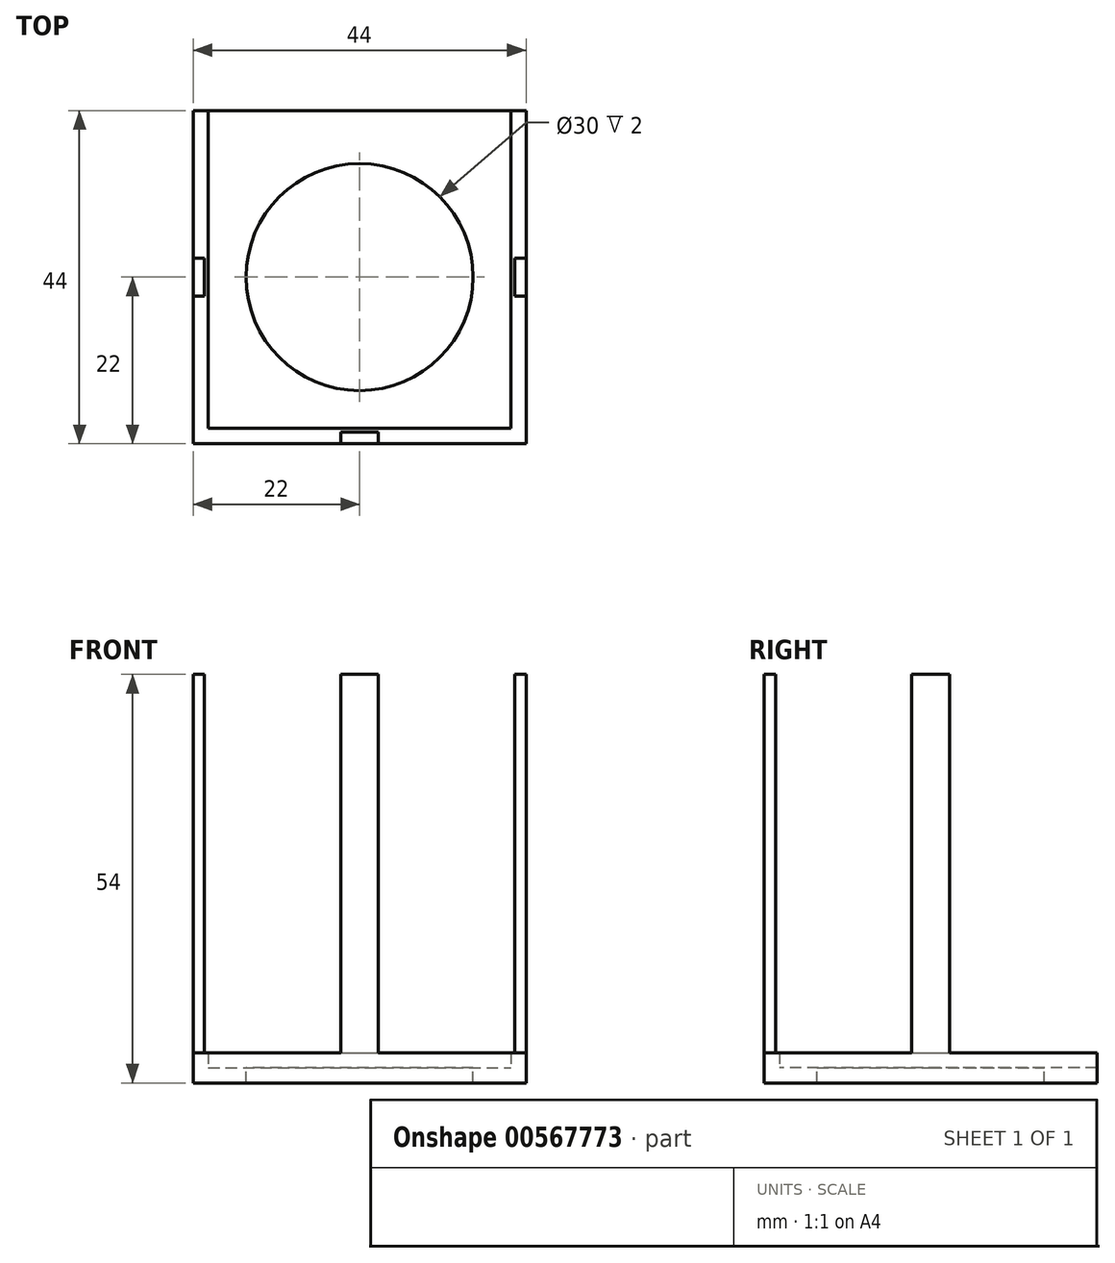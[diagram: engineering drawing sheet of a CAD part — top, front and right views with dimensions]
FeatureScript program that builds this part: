
annotation { "Feature Type Name" : "Feature", "Feature Type Description" : "" }
export const myFeature = defineFeature(function(context is Context, id is Id, definition is map)
    precondition{}
    {
        {
            var Q0;
            Q0=qCreatedBy(makeId("Top.planeOp"),FACE);
            var sketch = newSketch(context, id + "F0", { "sketchPlane" : qUnion([Q0])});
            skLineSegment(sketch, "E0.bottom", {"start": v(-22, 22) * mm, "end": v(22, 22) * mm});
            skLineSegment(sketch, "E0.top", {"start": v(-22, -22) * mm, "end": v(22, -22) * mm});
            skLineSegment(sketch, "E0.left", {"start": v(-22, 22) * mm, "end": v(-22, -22) * mm});
            skLineSegment(sketch, "E0.right", {"start": v(22, 22) * mm, "end": v(22, -22) * mm});
            skPoint(sketch, "E0.middle", {"position": v(0, 0) * mm});
            skCircle(sketch, "E1", {"center": v(0, 0) * mm, "radius": 15 * mm});
            skLineSegment(sketch, "E2", {"start": v(-20, 22) * mm, "end": v(-20, -20) * mm});
            skLineSegment(sketch, "E3", {"start": v(-20, -20) * mm, "end": v(20, -20) * mm});
            skLineSegment(sketch, "E4", {"start": v(20, -20) * mm, "end": v(20, 22) * mm});
            skSolve(sketch);
        }
        {
            var Q0;
            Q0=makeQuery(id+"F0.imprint","IMPRINT",FACE,{"disambiguationData":[TD([[makeQuery(id+"F0.imprint","IMPRINT",EDGE,{"derivedFrom":sQuery(id+"F0.wireOp",EDGE,"E1")}),-1.0]])]});
            var Q1;
            Q1=makeQuery(id+"F0.imprint","IMPRINT",FACE,{"disambiguationData":[TD([[makeQuery(id+"F0.imprint","IMPRINT",EDGE,{"derivedFrom":sQuery(id+"F0.wireOp",EDGE,"E0.bottom")}),-1.0]])]});
            extrude(context, id + "F1", {"entities" : qUnion([Q0, Q1]), "oppositeDirection" : true, "depth" : 2 * mm, "offsetDistance" : 25 * mm});
        }
        {
            var Q0;
            Q0=makeQuery(id+"F0.imprint","IMPRINT",FACE,{"disambiguationData":[TD([[makeQuery(id+"F0.imprint","IMPRINT",EDGE,{"derivedFrom":sQuery(id+"F0.wireOp",EDGE,"E0.top")}),1.0]])]});
            extrude(context, id + "F2", {"entities" : qUnion([Q0]), "operationType" : NewBodyOperationType.ADD, "depth" : 2 * mm, "offsetDistance" : 25 * mm});
        }
        {
            var Q0;
            Q0=makeQuery(id+"F2.opExtrude","CAP_FACE",FACE,{"disambiguationData":[OSD([sQuery(id+"F0.wireOp",EDGE,"E0.bottom"),sQuery(id+"F0.wireOp",EDGE,"E0.top"),sQuery(id+"F0.wireOp",EDGE,"E0.left"),sQuery(id+"F0.wireOp",EDGE,"E0.right"),sQuery(id+"F0.wireOp",EDGE,"E2"),sQuery(id+"F0.wireOp",EDGE,"E3"),sQuery(id+"F0.wireOp",EDGE,"E4")])],"isStart":false});
            var sketch = newSketch(context, id + "F3", { "sketchPlane" : qUnion([Q0])});
            skLineSegment(sketch, "E5.bottom", {"start": v(-22, 2.5) * mm, "end": v(-20.5, 2.5) * mm});
            skLineSegment(sketch, "E5.top", {"start": v(-22, -2.5) * mm, "end": v(-20.5, -2.5) * mm});
            skLineSegment(sketch, "E5.left", {"start": v(-22, 2.5) * mm, "end": v(-22, -2.5) * mm});
            skLineSegment(sketch, "E5.right", {"start": v(-20.5, 2.5) * mm, "end": v(-20.5, -2.5) * mm});
            skPoint(sketch, "E5.middle", {"position": v(-21.25, 0) * mm});
            skLineSegment(sketch, "E6.1.0", {"start": v(-2.5, -20.5) * mm, "end": v(2.5, -20.5) * mm});
            skPoint(sketch, "E6.1.1", {"position": v(0, -21.25) * mm});
            skLineSegment(sketch, "E6.1.2", {"start": v(-2.5, -22) * mm, "end": v(2.5, -22) * mm});
            skLineSegment(sketch, "E6.1.3", {"start": v(2.5, -22) * mm, "end": v(2.5, -20.5) * mm});
            skLineSegment(sketch, "E6.1.4", {"start": v(-2.5, -22) * mm, "end": v(-2.5, -20.5) * mm});
            skLineSegment(sketch, "E6.2.0", {"start": v(20.5, -2.5) * mm, "end": v(20.5, 2.5) * mm});
            skPoint(sketch, "E6.2.1", {"position": v(21.25, 0) * mm});
            skLineSegment(sketch, "E6.2.2", {"start": v(22, -2.5) * mm, "end": v(22, 2.5) * mm});
            skLineSegment(sketch, "E6.2.3", {"start": v(22, 2.5) * mm, "end": v(20.5, 2.5) * mm});
            skLineSegment(sketch, "E6.2.4", {"start": v(22, -2.5) * mm, "end": v(20.5, -2.5) * mm});
            skLineSegment(sketch, "E6.3.0", {"start": v(2.5, 20.5) * mm, "end": v(-2.5, 20.5) * mm});
            skPoint(sketch, "E6.3.1", {"position": v(0, 21.25) * mm});
            skLineSegment(sketch, "E6.3.2", {"start": v(2.5, 22) * mm, "end": v(-2.5, 22) * mm});
            skLineSegment(sketch, "E6.3.3", {"start": v(-2.5, 22) * mm, "end": v(-2.5, 20.5) * mm});
            skLineSegment(sketch, "E6.3.4", {"start": v(2.5, 22) * mm, "end": v(2.5, 20.5) * mm});
            skPoint(sketch, "E6.center", {"position": v(0, 0) * mm});
            skSolve(sketch);
        }
        {
            var Q0;
            Q0=makeQuery(id+"F3.imprint","IMPRINT",FACE,{"disambiguationData":[TD([[makeQuery(id+"F3.imprint","IMPRINT",EDGE,{"derivedFrom":sQuery(id+"F3.wireOp",EDGE,"E5.bottom")}),-1.0]])]});
            var Q1;
            Q1=makeQuery(id+"F3.imprint","IMPRINT",FACE,{"disambiguationData":[TD([[makeQuery(id+"F3.imprint","IMPRINT",EDGE,{"derivedFrom":sQuery(id+"F3.wireOp",EDGE,"E6.1.0")}),-1.0]])]});
            var Q2;
            Q2=makeQuery(id+"F3.imprint","IMPRINT",FACE,{"disambiguationData":[TD([[makeQuery(id+"F3.imprint","IMPRINT",EDGE,{"derivedFrom":sQuery(id+"F3.wireOp",EDGE,"E6.2.0")}),-1.0]])]});
            extrude(context, id + "F4", {"entities" : qUnion([Q0, Q1, Q2]), "operationType" : NewBodyOperationType.ADD, "depth" : 50 * mm, "offsetDistance" : 25 * mm});
        }
    });
